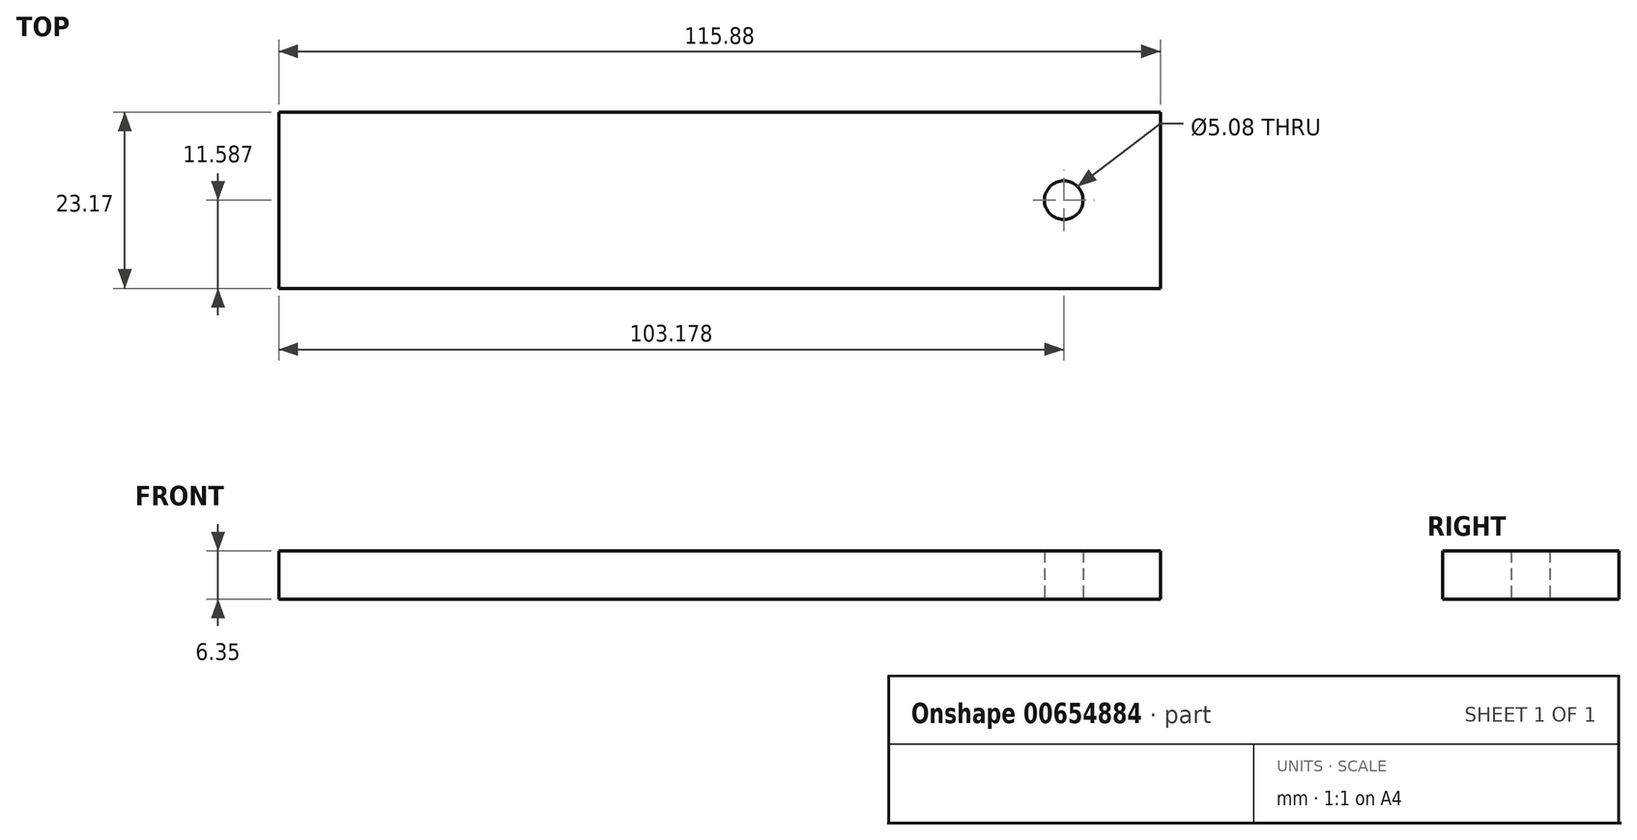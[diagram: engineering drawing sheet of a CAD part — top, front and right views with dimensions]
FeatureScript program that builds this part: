
annotation { "Feature Type Name" : "Feature", "Feature Type Description" : "" }
export const myFeature = defineFeature(function(context is Context, id is Id, definition is map)
    precondition{}
    {
        {
            var Q0;
            Q0=qCreatedBy(makeId("Top.planeOp"),FACE);
            var sketch = newSketch(context, id + "F0", { "sketchPlane" : qUnion([Q0])});
            skLineSegment(sketch, "E0", {"start": v(-56.39, 8.88) * mm, "end": v(59.49, 8.88) * mm});
            skLineSegment(sketch, "E1", {"start": v(-56.39, 32.05) * mm, "end": v(59.49, 32.05) * mm});
            skLineSegment(sketch, "E2", {"start": v(-56.39, 32.05) * mm, "end": v(-56.39, 8.88) * mm});
            skLineSegment(sketch, "E3", {"start": v(59.49, 32.05) * mm, "end": v(59.49, 8.88) * mm});
            skSolve(sketch);
        }
        {
            var Q0;
            Q0=makeQuery(id+"F0.imprint","IMPRINT",FACE,{"disambiguationData":[TD([[makeQuery(id+"F0.imprint","IMPRINT",EDGE,{"derivedFrom":sQuery(id+"F0.wireOp",EDGE,"E0")}),1.0]])]});
            extrude(context, id + "F1", {"entities" : qUnion([Q0]), "depth" : 6.35 * mm, "offsetDistance" : 25.4 * mm});
        }
        {
            var Q0;
            Q0=qCreatedBy(makeId("Top.planeOp"),FACE);
            var sketch = newSketch(context, id + "F2", { "sketchPlane" : qUnion([Q0])});
            skCircle(sketch, "E4", {"center": v(46.79, 20.47) * mm, "radius": 2.54 * mm});
            skSolve(sketch);
        }
        {
            var Q0;
            Q0=sQuery(id+"F2.wireOp",VERTEX,"E4.center");
            var Q1;
            Q1=makeQuery(id+"F1.opExtrude","SWEPT_BODY",BODY,{"disambiguationData":[OSD([sQuery(id+"F0.wireOp",EDGE,"E0"),sQuery(id+"F0.wireOp",EDGE,"E1"),sQuery(id+"F0.wireOp",EDGE,"E2"),sQuery(id+"F0.wireOp",EDGE,"E3")])]});
            hole(context, id + "F3", {"style" : HoleStyle.SIMPLE, "endStyle" : HoleEndStyle.THROUGH, "oppositeDirection" : true, "holeDiameter" : 5.08 * mm, "majorDiameter" : 6.35 * mm, "isTappedThrough" : true, "tappedDepth" : 12.7 * mm, "tapClearance" : 3, "locations" : qUnion([Q0]), "scope" : qUnion([Q1])});
        }
    });
